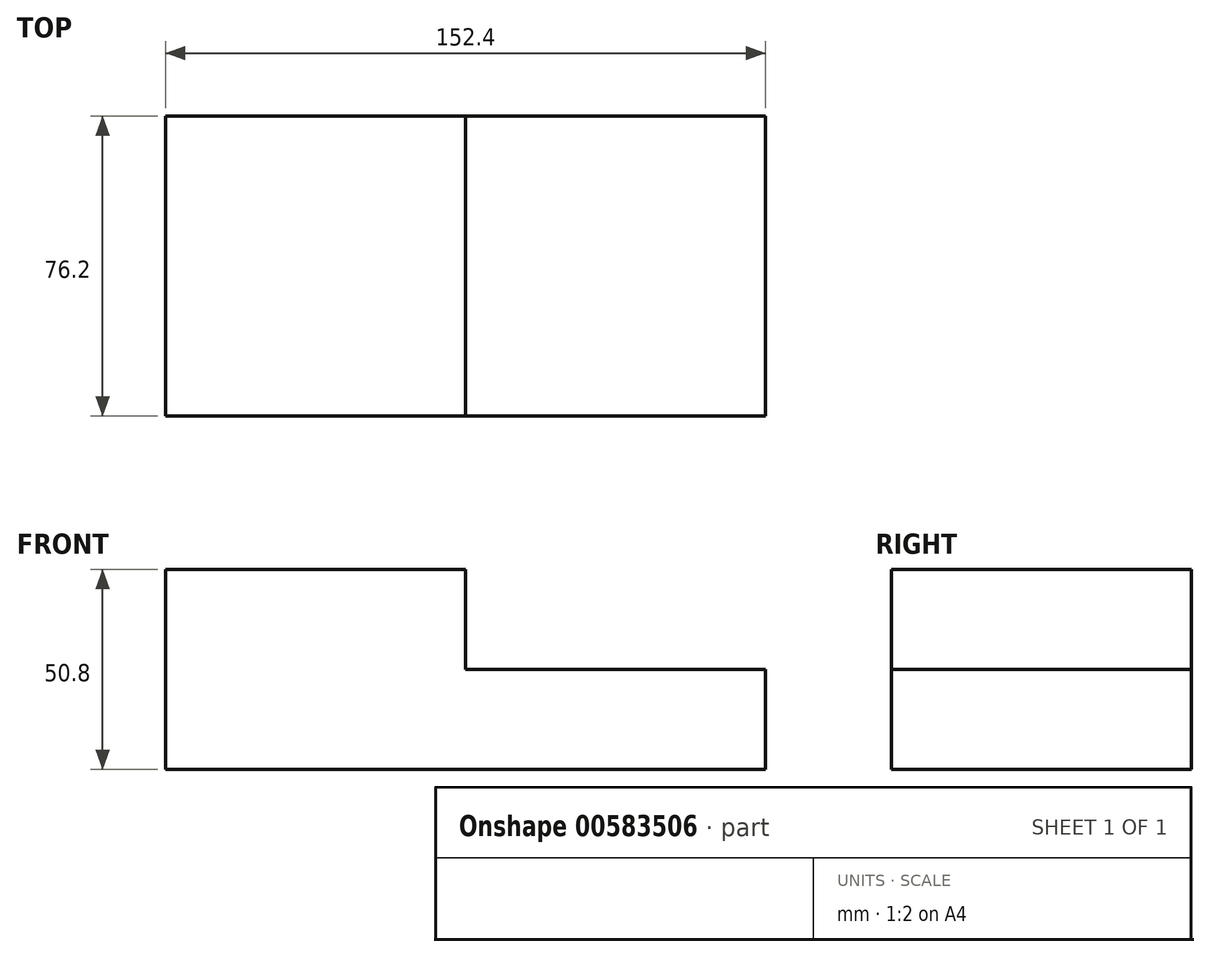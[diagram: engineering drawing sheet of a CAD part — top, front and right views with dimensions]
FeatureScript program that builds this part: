
annotation { "Feature Type Name" : "Feature", "Feature Type Description" : "" }
export const myFeature = defineFeature(function(context is Context, id is Id, definition is map)
    precondition{}
    {
        {
            var Q0;
            Q0=qCreatedBy(makeId("Front.planeOp"),FACE);
            var sketch = newSketch(context, id + "F0", { "sketchPlane" : qUnion([Q0])});
            skLineSegment(sketch, "E0", {"start": v(0, 0) * mm, "end": v(0, 50.8) * mm});
            skLineSegment(sketch, "E1", {"start": v(0, 50.8) * mm, "end": v(76.2, 50.8) * mm});
            skLineSegment(sketch, "E2", {"start": v(76.2, 50.8) * mm, "end": v(76.2, 25.4) * mm});
            skLineSegment(sketch, "E3", {"start": v(76.2, 25.4) * mm, "end": v(152.4, 25.4) * mm});
            skLineSegment(sketch, "E4", {"start": v(152.4, 25.4) * mm, "end": v(152.4, 0) * mm});
            skLineSegment(sketch, "E5", {"start": v(152.4, 0) * mm, "end": v(0, 0) * mm});
            skSolve(sketch);
        }
        {
            var Q0;
            Q0=makeQuery(id+"F0.imprint","IMPRINT",FACE,{"disambiguationData":[TD([[makeQuery(id+"F0.imprint","IMPRINT",EDGE,{"derivedFrom":sQuery(id+"F0.wireOp",EDGE,"E0")}),-1.0]])]});
            extrude(context, id + "F1", {"entities" : qUnion([Q0]), "depth" : 76.2 * mm, "offsetDistance" : 25.4 * mm});
        }
    });
